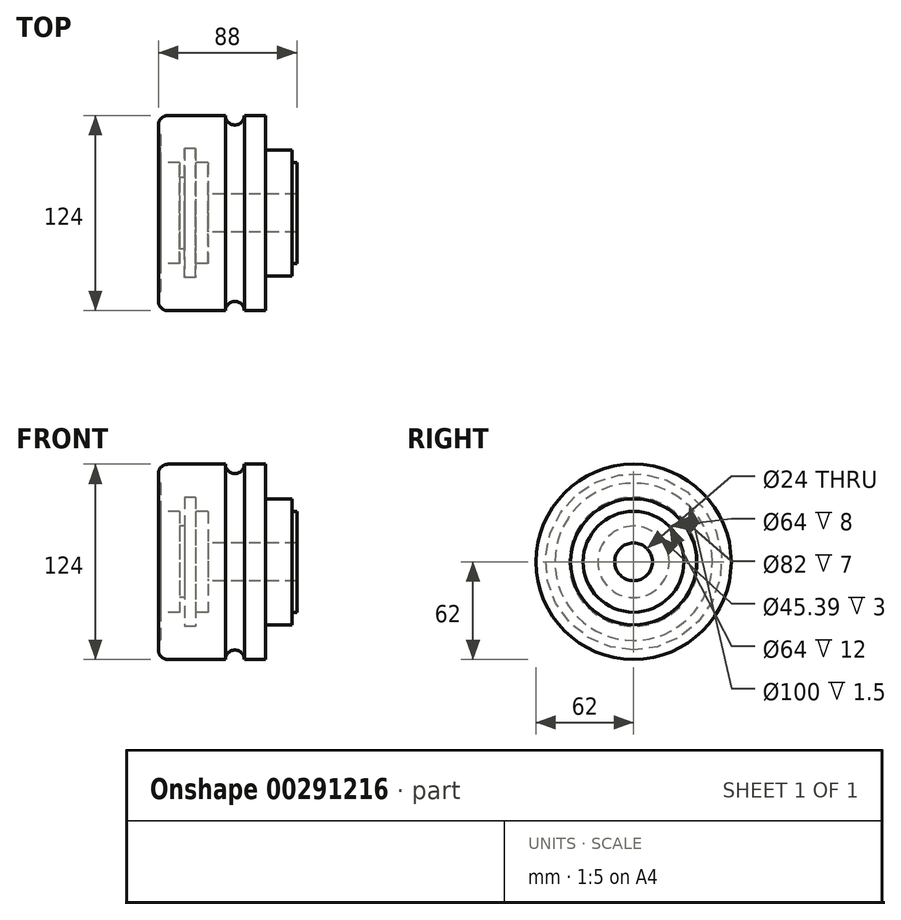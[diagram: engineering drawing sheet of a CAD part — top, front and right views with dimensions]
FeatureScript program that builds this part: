
annotation { "Feature Type Name" : "Feature", "Feature Type Description" : "" }
export const myFeature = defineFeature(function(context is Context, id is Id, definition is map)
    precondition{}
    {
        {
            var Q0;
            Q0=qCreatedBy(makeId("Front.planeOp"),FACE);
            var sketch = newSketch(context, id + "F0", { "sketchPlane" : qUnion([Q0])});
            skLineSegment(sketch, "E0", {"start": v(0, 0) * mm, "end": v(0, 62) * mm});
            skLineSegment(sketch, "E1", {"start": v(0, 62) * mm, "end": v(42.57, 62) * mm});
            skLineSegment(sketch, "E2", {"start": v(68, 62) * mm, "end": v(68, 40) * mm});
            skLineSegment(sketch, "E3", {"start": v(68, 40) * mm, "end": v(85, 40) * mm});
            skLineSegment(sketch, "E4", {"start": v(85, 40) * mm, "end": v(85, 32) * mm});
            skLineSegment(sketch, "E5", {"start": v(85, 32) * mm, "end": v(88, 32) * mm});
            skLineSegment(sketch, "E6", {"start": v(88, 32) * mm, "end": v(88, 0) * mm});
            skLineSegment(sketch, "E7", {"start": v(0, 0) * mm, "end": v(88, 0) * mm});
            skLineSegment(sketch, "E8", {"start": v(0, 0) * mm, "end": v(-30.14, 0) * mm, "construction": true});
            skArc(sketch, "E9", {"start": v(42.57, 62) * mm, "mid": v(48.57, 56) * mm, "end": v(54.57, 62) * mm});
            skLineSegment(sketch, "E10.trimOffspring", {"start": v(54.57, 62) * mm, "end": v(68, 62) * mm});
            skSolve(sketch);
        }
        {
            var Q0;
            Q0 = qSketchRegion(id + "F0", true);
            var Q1;
            Q1=sQuery(id+"F0.wireOp",EDGE,"E8");
            revolve(context, id + "F1", {"entities" : qUnion([Q0]), "axis" : qUnion([Q1]), "revolveType" : RevolveType.FULL});
        }
        {
            var Q0;
            Q0=qCreatedBy(makeId("Front.planeOp"),FACE);
            var sketch = newSketch(context, id + "F2", { "sketchPlane" : qUnion([Q0])});
            skLineSegment(sketch, "E11", {"start": v(0, 0) * mm, "end": v(0, 50) * mm});
            skLineSegment(sketch, "E12", {"start": v(0, 50) * mm, "end": v(1.5, 50) * mm});
            skLineSegment(sketch, "E13", {"start": v(1.5, 50) * mm, "end": v(1.5, 32) * mm});
            skLineSegment(sketch, "E14", {"start": v(1.5, 32) * mm, "end": v(13.5, 32) * mm});
            skLineSegment(sketch, "E15", {"start": v(13.5, 32) * mm, "end": v(13.5, 22.7) * mm});
            skLineSegment(sketch, "E16", {"start": v(13.5, 22.7) * mm, "end": v(16.5, 22.7) * mm});
            skLineSegment(sketch, "E17", {"start": v(16.5, 22.7) * mm, "end": v(16.5, 41) * mm});
            skLineSegment(sketch, "E18", {"start": v(16.5, 41) * mm, "end": v(23.5, 41) * mm});
            skLineSegment(sketch, "E19", {"start": v(23.5, 41) * mm, "end": v(23.5, 32) * mm});
            skLineSegment(sketch, "E20", {"start": v(23.5, 32) * mm, "end": v(31.5, 32) * mm});
            skLineSegment(sketch, "E21", {"start": v(31.5, 32) * mm, "end": v(31.5, 12) * mm});
            skLineSegment(sketch, "E22", {"start": v(31.5, 12) * mm, "end": v(88, 12) * mm});
            skLineSegment(sketch, "E23", {"start": v(88, 12) * mm, "end": v(88, 0) * mm});
            skLineSegment(sketch, "E24", {"start": v(88, 0) * mm, "end": v(0, 0) * mm});
            skLineSegment(sketch, "E25", {"start": v(0, 50) * mm, "end": v(0, 0) * mm});
            skLineSegment(sketch, "E26", {"start": v(0, 0) * mm, "end": v(88, 0) * mm});
            skLineSegment(sketch, "E27", {"start": v(0, 0) * mm, "end": v(-30.72, 0) * mm, "construction": true});
            skSolve(sketch);
        }
        {
            var Q0;
            Q0 = qSketchRegion(id + "F2", true);
            var Q1;
            Q1=sQuery(id+"F2.wireOp",EDGE,"E27");
            revolve(context, id + "F3", {"operationType" : NewBodyOperationType.REMOVE, "entities" : qUnion([Q0]), "axis" : qUnion([Q1]), "revolveType" : RevolveType.FULL, "oppositeDirection" : true});
        }
        {
            var Q0;
            Q0=makeQuery(id+"F1.opRevolve","SWEPT_EDGE",EDGE,{"disambiguationData":[OSD([sQuery(id+"F0.wireOp",EDGE,"E0"),sQuery(id+"F0.wireOp",EDGE,"E1")])]});
            fillet(context, id + "F4", {"entities" : qUnion([Q0]), "radius" : 6 * mm, "tangentPropagation" : true, "allowEdgeOverflow" : false});
        }
    });
